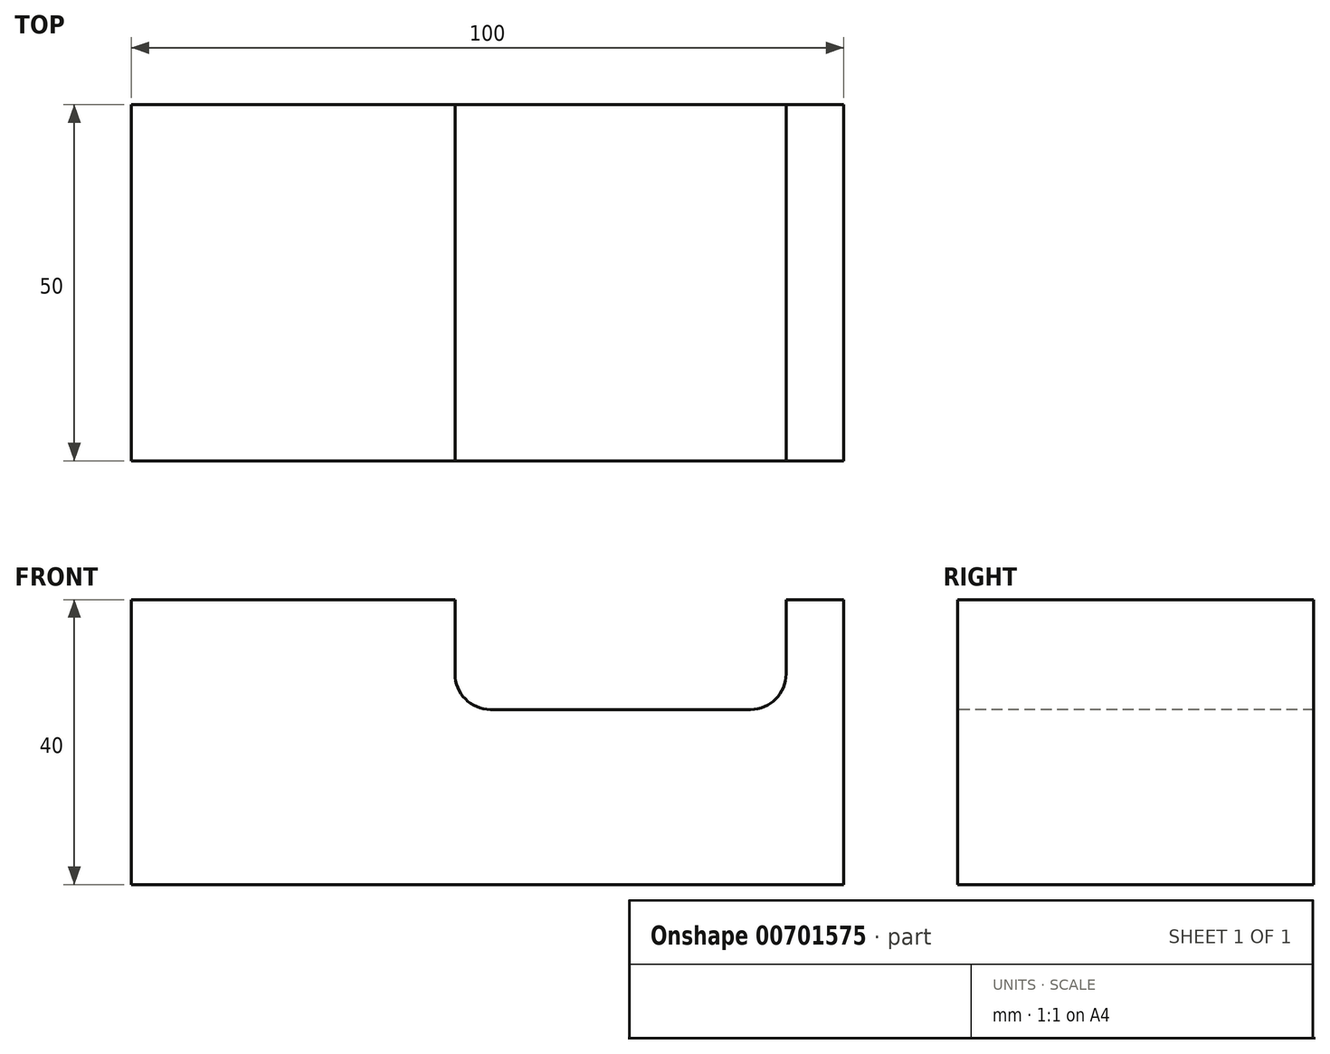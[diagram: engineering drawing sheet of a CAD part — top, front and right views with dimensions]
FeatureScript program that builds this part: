
annotation { "Feature Type Name" : "Feature", "Feature Type Description" : "" }
export const myFeature = defineFeature(function(context is Context, id is Id, definition is map)
    precondition{}
    {
        {
            var Q0;
            Q0=qCreatedBy(makeId("Top.planeOp"),FACE);
            var sketch = newSketch(context, id + "F0", { "sketchPlane" : qUnion([Q0])});
            skLineSegment(sketch, "E0.bottom", {"start": v(-50, 25) * mm, "end": v(50, 25) * mm});
            skLineSegment(sketch, "E0.top", {"start": v(-50, -25) * mm, "end": v(50, -25) * mm});
            skLineSegment(sketch, "E0.left", {"start": v(-50, 25) * mm, "end": v(-50, -25) * mm});
            skLineSegment(sketch, "E0.right", {"start": v(50, 25) * mm, "end": v(50, -25) * mm});
            skPoint(sketch, "E0.middle", {"position": v(0, 0) * mm});
            skSolve(sketch);
        }
        {
            var Q0;
            Q0 = qSketchRegion(id + "F0", true);
            extrude(context, id + "F1", {"entities" : qUnion([Q0]), "depth" : 40 * mm, "offsetDistance" : 25 * mm});
        }
        {
            var Q0;
            Q0=makeQuery(id+"F1.opExtrude","SWEPT_FACE",FACE,{"disambiguationData":[OSD([sQuery(id+"F0.wireOp",EDGE,"E0.top")])]});
            var sketch = newSketch(context, id + "F2", { "sketchPlane" : qUnion([Q0])});
            skLineSegment(sketch, "E1.bottom", {"start": v(-4.57, 54.99) * mm, "end": v(41.93, 54.99) * mm});
            skLineSegment(sketch, "E1.top", {"start": v(-4.57, 24.59) * mm, "end": v(41.93, 24.59) * mm});
            skLineSegment(sketch, "E1.left", {"start": v(-4.57, 54.99) * mm, "end": v(-4.57, 24.59) * mm});
            skLineSegment(sketch, "E1.right", {"start": v(41.93, 54.99) * mm, "end": v(41.93, 24.59) * mm});
            skSolve(sketch);
        }
        {
            var Q0;
            Q0 = qSketchRegion(id + "F2", true);
            extrude(context, id + "F3", {"entities" : qUnion([Q0]), "operationType" : NewBodyOperationType.REMOVE, "oppositeDirection" : true, "depth" : 99 * mm, "offsetDistance" : 25 * mm});
        }
        {
            var Q0;
            Q0=makeQuery(id+"F3.boolean.opBoolean","COPY",EDGE,{"derivedFrom":makeQuery(id+"F3.opExtrude","SWEPT_EDGE",EDGE,{"disambiguationData":[OSD([sQuery(id+"F2.wireOp",EDGE,"E1.top"),sQuery(id+"F2.wireOp",EDGE,"E1.left")])]})});
            var Q1;
            Q1=makeQuery(id+"F3.boolean.opBoolean","COPY",EDGE,{"derivedFrom":makeQuery(id+"F3.opExtrude","SWEPT_EDGE",EDGE,{"disambiguationData":[OSD([sQuery(id+"F2.wireOp",EDGE,"E1.top"),sQuery(id+"F2.wireOp",EDGE,"E1.right")])]})});
            fillet(context, id + "F4", {"entities" : qUnion([Q0, Q1]), "radius" : 5 * mm, "tangentPropagation" : true, "allowEdgeOverflow" : false});
        }
    });
